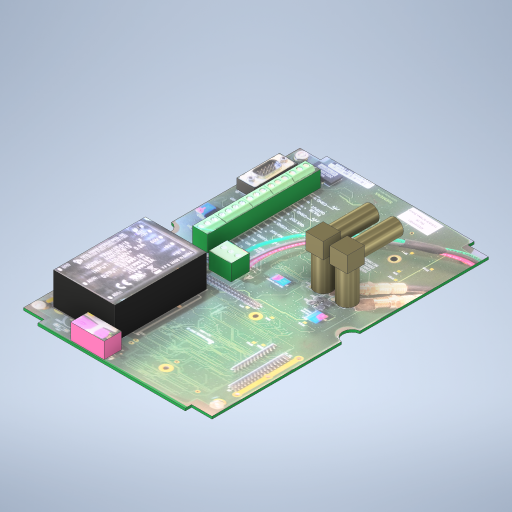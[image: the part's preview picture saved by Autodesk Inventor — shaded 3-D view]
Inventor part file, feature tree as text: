
AUTODESK INVENTOR PART (.ipt)
format: ipt  version: 2024 (Build 280153000, 153)  size: 17,443,840 bytes
history: native  units: in
note: dims shown in document units (in); Inventor stores cm internally (conversion verified against a paired STEP export)
features: sketch x14, other x11, extrude x10
ambient origin geometry x8: Origin, YZ Plane, XZ Plane, XY Plane, X Axis, Y Axis, Z Axis, Center Point
bodies: Solid1 (feature_tree)
feature tree (35):
  extrude  "Extrusion1"  Depth=5.9055in
  extrude  "Extrusion2"  Depth=0.0787in TaperAngle=0.0deg
  other  "Decal1"
  extrude  "Extrusion3"  Depth=0.5in TaperAngle=0.0deg
  other  "Decal2"
  extrude  "Extrusion4"  Depth=1.0in TaperAngle=0.0deg
  sketch  "Sketch7"  dims[d39=1.25in d40=0.0in d41=2.0in d42=0.0in]
  other  "Decal4"
  other  "Decal5"
  extrude  "Extrusion5"  Depth=0.5in TaperAngle=0.0deg
  other  "Decal6"
  extrude  "Extrusion6"  Depth=1.25in TaperAngle=0.0deg
  extrude  "Extrusion7"  [1 undecoded]
  extrude  "Extrusion10"  [1 undecoded]
  other  "Decal7"
  extrude  "Extrusion13"  [1 undecoded]
  extrude  "Extrusion14"  [1 undecoded]
  sketch  "Sketch2"  dims[d0=9.0551in d1=5.9055in]
  sketch  "Sketch3"  dims[d2=0.0787in d3=0.0in d4=0.0787in d5=0.0in]
  other  "Image1"
  sketch  "Sketch4"  dims[d14=1.0in d15=0.0in d17=0.5in d18=0.0in]
  sketch  "Sketch5"  dims[d20=0.3in d21=0.0in d23=1.0in d24=0.0in]
  other  "Image2"
  sketch  "Sketch6"  dims[d25=0.5in d26=0.0in d31=0.5in d32=0.0in]
  other  "Image3"
  sketch  "Sketch8"
  sketch  "Sketch9"
  other  "Image4"
  sketch  "Sketch10"
  sketch  "Sketch11"
  sketch  "Sketch14"
  sketch  "Sketch15"
  other  "Image5"
  sketch  "Sketch18"
  sketch  "Sketch19"
note: 4 required parameter values undecoded (feature->parameter linkage not recoverable at this tier; creation-order binding heuristic only, values carry confidence <= 0.55)
